# Revit family: Gira_102300
name_source: partatom
category: Elektroinstallationen
revit_build: Autodesk Revit 2017 (Build: 20160225_1515(x64)
units: mm (PartAtom-declared; Revit-internal decimal feet)

## family parameters
Basisbauteil = Fläche
Beim Laden mit Abzugskörper schneiden = Nein
Bemaßung runder Anschluss = Durchmesser verwenden
Beschriftungsausrichtung beibehalten = Nein
Gemeinsam genutzt = Nein
Raumberechnungspunkt = Nein
Teiletyp = Normal

## types (1)
- Gira_102300
    BIM = https://media.stage.bim.site X1 REG KNX.rfa
    Beschreibung = Area line coup.line ampl.DRA KNX,KNX area line coupler or line amplifier,,DRA plus,Features:,- The area line coupler connects two KNX lines to each other for data transfer and ensures electrical isolation between these lines. As a result, each bus line of a KNX installation can be operated electrically independently of the other lines.,Area line coupler:,- Use as an area or line coupler, depending on the specification of the physical address and parameterisation.,- Reduction of the bus load via filter function (filter table).,- Forwarding of group telegrams can be parameterised.,- Repetition rate in the case of transfer errors.,- Telegram confirmation can be parameterised.,- Support of the completely expanded group address area from 0 to 31 with the functions block", "forward unfiltered", and "filter" in both communication directions between the main and subline.,- "Forward unfiltered" and "block" functions can also be selected for physically addressed telegrams between main and subline in both communication directions (programming and tamper protection).,- "Repeat: yes no" function can be set separately in case of transfer errors on the main or subline for the telegram type "Broadcast".,- Telegram confirmation on the main and subline possible separately for group telegrams and physically addressed telegrams with the settings "always" and "for forwarding only".,- For physically addressed telegrams, the setting "always reject NACK (Not-Acknowledge)" can be selected (programming protection with feedback).,Line amplifier:,- As a line amplifier, extending the lines to max. four line segments (max. three line amplifiers per line connected in parallel per line) with up to 64 devices each is possible.,- Repetition rate in the case of transfer errors.,,Notes :,- A separate power supply is required for each line (area line, main line, line) or each line segment."
    Bus system KNX = Ja
    Bus system KNX radio = Nein
    Bus system LON = Nein
    Bus system Powernet = Nein
    Bus system radio frequent = Nein
    Data sheet = https://katalog.gira.de
    GTIN = 4010337040798
    HAN = 102300
    Hersteller = Gira
    Mounting method = DRA (DIN-rail adapter)
    Other bus systems = None
    Productwebsite = http://katalog.gira.de
    Typname = Area/line coup. line ampl. KNX DRA
    URL = https://www.gira.de
    Vorgabe-Ansicht = 1219 mm
    Width in number of modular spacings = 2

## geometry (parser evidence)
native form markers: Sweep x2
no freeform markers — native parametric forms only
